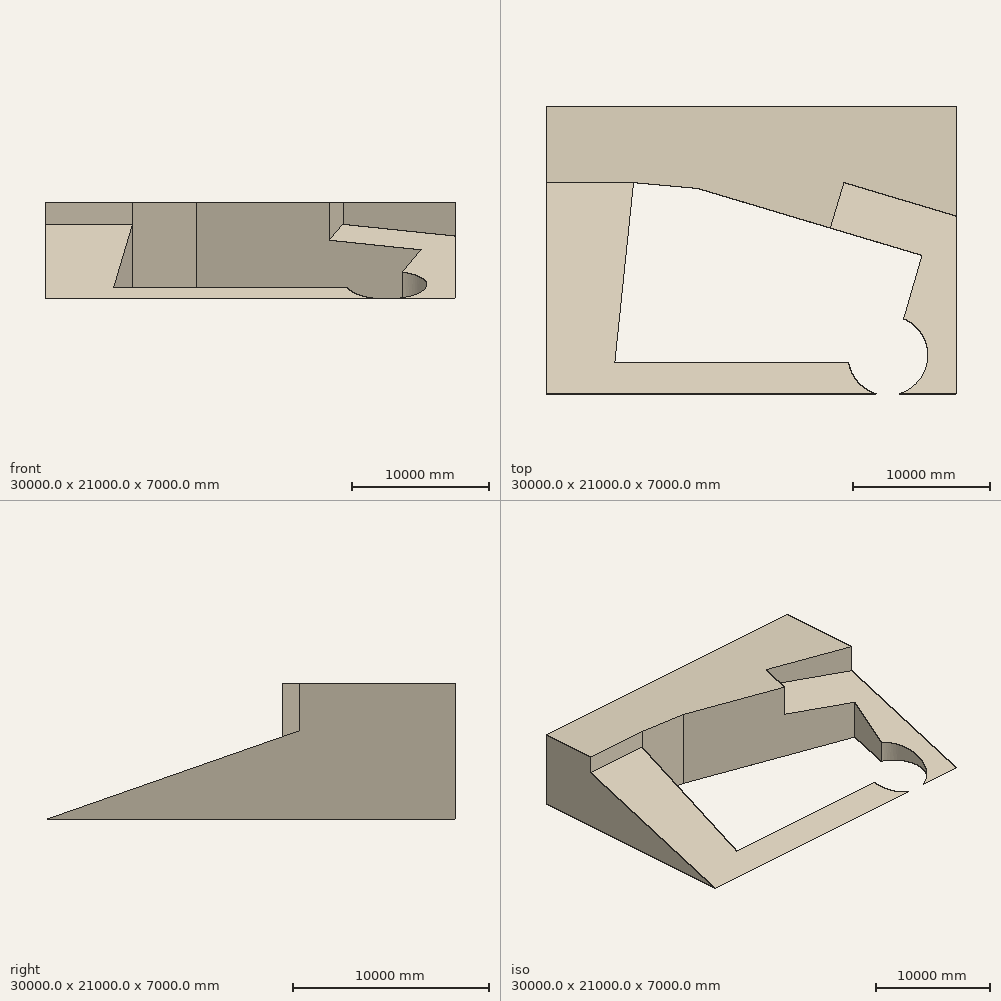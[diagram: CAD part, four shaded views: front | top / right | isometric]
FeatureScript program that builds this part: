
annotation { "Feature Type Name" : "Feature", "Feature Type Description" : "" }
export const myFeature = defineFeature(function(context is Context, id is Id, definition is map)
    precondition{}
    {
        {
            var Q0;
            Q0=qCreatedBy(makeId("Top.planeOp"),FACE);
            var sketch = newSketch(context, id + "F0", { "sketchPlane" : qUnion([Q0])});
            skLineSegment(sketch, "E0", {"start": v(0, 0) * mm, "end": v(20210, 0) * mm, "construction": true});
            skLineSegment(sketch, "E1", {"start": v(20210, 0) * mm, "end": v(22485.16, 7836.4) * mm, "construction": true});
            skLineSegment(sketch, "E2", {"start": v(22485.16, 7836.4) * mm, "end": v(6071.14, 12737.09) * mm});
            skLineSegment(sketch, "E3", {"start": v(6071.14, 12737.09) * mm, "end": v(1370.92, 13168.83) * mm});
            skLineSegment(sketch, "E4", {"start": v(1370.92, 13168.83) * mm, "end": v(0, 0) * mm});
            skCircle(sketch, "E5", {"center": v(19983.2, 510) * mm, "radius": 2925 * mm, "construction": true});
            skArc(sketch, "E6", {"start": v(17103, 0) * mm, "mid": v(21799.7, -1782.59) * mm, "end": v(21138.27, 3197.27) * mm});
            skLineSegment(sketch, "E7", {"start": v(0, 0) * mm, "end": v(17103, 0) * mm});
            skLineSegment(sketch, "E8", {"start": v(21138.27, 3197.27) * mm, "end": v(22485.16, 7836.4) * mm});
            skSolve(sketch);
        }
        {
            var Q0;
            Q0=qCreatedBy(makeId("Right.planeOp"),FACE);
            var sketch = newSketch(context, id + "F1", { "sketchPlane" : qUnion([Q0])});
            skLineSegment(sketch, "E9", {"start": v(-2300, 0) * mm, "end": v(18700, 0) * mm});
            skLineSegment(sketch, "E10", {"start": v(17700, 7000) * mm, "end": v(-2300, 0) * mm});
            skLineSegment(sketch, "E11", {"start": v(7700, 0) * mm, "end": v(7700, 3500) * mm, "construction": true});
            skLineSegment(sketch, "E12", {"start": v(18700, 0) * mm, "end": v(18700, 7000) * mm});
            skLineSegment(sketch, "E13", {"start": v(18700, 7000) * mm, "end": v(17700, 7000) * mm});
            skSolve(sketch);
        }
        {
            var Q0;
            Q0=makeQuery(id+"F1.imprint","IMPRINT",FACE,{"disambiguationData":[TD([[makeQuery(id+"F1.imprint","IMPRINT",EDGE,{"derivedFrom":sQuery(id+"F1.wireOp",EDGE,"E9")}),1.0]])]});
            extrude(context, id + "F2", {"entities" : qUnion([Q0]), "depth" : 25000 * mm, "offsetDistance" : 25 * mm, "hasSecondDirection" : true, "secondDirectionOppositeDirection" : true, "secondDirectionDepth" : 5000 * mm});
        }
        {
            var Q0;
            Q0 = qSketchRegion(id + "F0", true);
            extrude(context, id + "F3", {"entities" : qUnion([Q0]), "operationType" : NewBodyOperationType.REMOVE, "endBound" : BoundingType.THROUGH_ALL, "depth" : 25 * mm, "offsetDistance" : 25 * mm});
        }
        {
            var Q0;
            Q0=makeQuery(id+"F2.opExtrude","SWEPT_FACE",FACE,{"disambiguationData":[OSD([sQuery(id+"F1.wireOp",EDGE,"E13")])]});
            var sketch = newSketch(context, id + "F4", { "sketchPlane" : qUnion([Q0])});
            skLineSegment(sketch, "E14", {"start": v(-5000, 17700) * mm, "end": v(25000, 17700) * mm});
            skLineSegment(sketch, "E15", {"start": v(15777.74, 9839.02) * mm, "end": v(6071.14, 12737.09) * mm});
            skLineSegment(sketch, "E16", {"start": v(6071.14, 12737.09) * mm, "end": v(1370.92, 13168.83) * mm});
            skLineSegment(sketch, "E17", {"start": v(1370.92, 13168.83) * mm, "end": v(-5000, 13168.83) * mm});
            skLineSegment(sketch, "E18", {"start": v(-5000, 13168.83) * mm, "end": v(-5000, 17700) * mm});
            skLineSegment(sketch, "E19", {"start": v(15777.74, 9839.02) * mm, "end": v(16771.9, 13168.83) * mm});
            skLineSegment(sketch, "E20", {"start": v(16771.9, 13168.83) * mm, "end": v(25000, 10712.2) * mm});
            skLineSegment(sketch, "E21", {"start": v(25000, 10712.2) * mm, "end": v(25000, 17700) * mm});
            skSolve(sketch);
        }
        {
            var Q0;
            Q0=makeQuery(id+"F4.imprint","IMPRINT",FACE,{"disambiguationData":[TD([[makeQuery(id+"F4.imprint","IMPRINT",EDGE,{"derivedFrom":sQuery(id+"F4.wireOp",EDGE,"E14")}),1.0]])]});
            extrude(context, id + "F5", {"entities" : qUnion([Q0]), "operationType" : NewBodyOperationType.ADD, "endBound" : BoundingType.UP_TO_NEXT, "oppositeDirection" : true, "depth" : 25 * mm, "offsetDistance" : 25 * mm});
        }
    });
